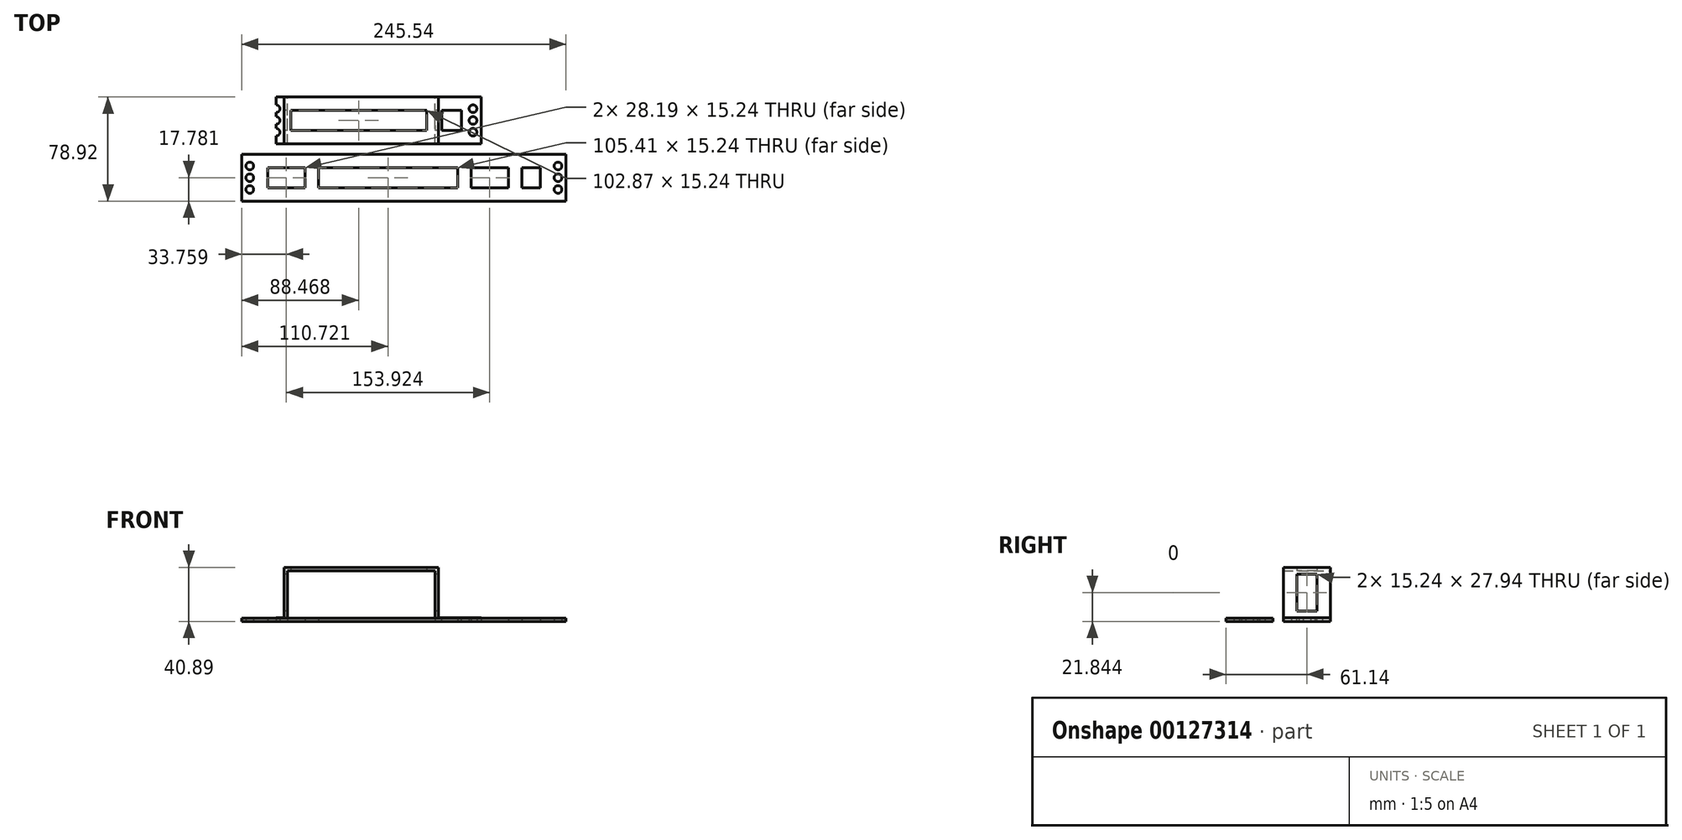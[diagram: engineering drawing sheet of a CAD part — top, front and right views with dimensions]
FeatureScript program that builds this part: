
annotation { "Feature Type Name" : "Feature", "Feature Type Description" : "" }
export const myFeature = defineFeature(function(context is Context, id is Id, definition is map)
    precondition{}
    {
        {
            var Q0;
            Q0=qCreatedBy(makeId("Top.planeOp"),FACE);
            var sketch = newSketch(context, id + "F0", { "sketchPlane" : qUnion([Q0])});
            skLineSegment(sketch, "E0.left", {"start": v(80.6, 17.78) * mm, "end": v(80.6, -17.78) * mm});
            skLineSegment(sketch, "E0.right", {"start": v(-80.6, 17.78) * mm, "end": v(-80.6, -17.78) * mm});
            skPoint(sketch, "E0.middle", {"position": v(0, 0) * mm});
            skLineSegment(sketch, "E1.left", {"start": v(66.03, 7.62) * mm, "end": v(66.03, -7.62) * mm});
            skLineSegment(sketch, "E1.right", {"start": v(-66.03, 7.62) * mm, "end": v(-66.03, -7.62) * mm});
            skLineSegment(sketch, "E2", {"start": v(-66.03, 7.62) * mm, "end": v(-66.03, 17.78) * mm});
            skLineSegment(sketch, "E3", {"start": v(-66.03, 17.78) * mm, "end": v(-66.03, -17.78) * mm});
            skLineSegment(sketch, "E4", {"start": v(66.03, 7.62) * mm, "end": v(66.03, 17.78) * mm});
            skLineSegment(sketch, "E5", {"start": v(66.03, 17.78) * mm, "end": v(66.03, -17.78) * mm});
            skLineSegment(sketch, "E6", {"start": v(-74.55, 17.78) * mm, "end": v(-74.55, -17.78) * mm});
            skLineSegment(sketch, "E7", {"start": v(-80.6, 0) * mm, "end": v(-80.6, -8.9) * mm});
            skCircle(sketch, "E8", {"center": v(-74.55, 8.9) * mm, "radius": 2.92 * mm});
            skCircle(sketch, "E9", {"center": v(-74.55, 0) * mm, "radius": 2.92 * mm});
            skCircle(sketch, "E10", {"center": v(-74.55, -8.9) * mm, "radius": 2.92 * mm});
            skCircle(sketch, "E11.MirrorC", {"center": v(74.55, 8.9) * mm, "radius": 2.92 * mm});
            skCircle(sketch, "E12.MirrorC", {"center": v(74.55, 0) * mm, "radius": 2.92 * mm});
            skCircle(sketch, "E13.MirrorC", {"center": v(74.55, -8.9) * mm, "radius": 2.92 * mm});
            skLineSegment(sketch, "E14", {"start": v(-80.6, 17.78) * mm, "end": v(-66.03, 17.78) * mm});
            skLineSegment(sketch, "E15", {"start": v(-66.03, -17.78) * mm, "end": v(-80.6, -17.78) * mm});
            skLineSegment(sketch, "E16", {"start": v(66.03, 17.78) * mm, "end": v(80.6, 17.78) * mm});
            skLineSegment(sketch, "E17", {"start": v(80.6, -17.78) * mm, "end": v(66.03, -17.78) * mm});
            skLineSegment(sketch, "E18.bottom", {"start": v(-66.03, 17.78) * mm, "end": v(66.03, 17.78) * mm});
            skLineSegment(sketch, "E18.top", {"start": v(-66.03, -17.78) * mm, "end": v(66.03, -17.78) * mm});
            skLineSegment(sketch, "E19.top", {"start": v(66.03, -7.62) * mm, "end": v(-66.03, -7.62) * mm});
            skLineSegment(sketch, "E20", {"start": v(39.38, 17.78) * mm, "end": v(39.38, -17.78) * mm});
            skLineSegment(sketch, "E21", {"start": v(-66.03, 7.62) * mm, "end": v(39.38, 7.62) * mm});
            skLineSegment(sketch, "E22", {"start": v(39.38, 7.62) * mm, "end": v(66.03, 7.62) * mm});
            skSolve(sketch);
        }
        {
            var Q0;
            {var subQ5=sQuery(id+"F0.wireOp",EDGE,"E21");Q0=makeQuery(id+"F0.imprint","IMPRINT",FACE,{"disambiguationData":[TD([[makeQuery(id+"F0.imprint","IMPRINT",EDGE,{"derivedFrom":subQ5}),1.0]])]});}
            var Q1;
            {var subQ8=sQuery(id+"F0.wireOp",EDGE,"E1.right");Q1=makeQuery(id+"F0.imprint","IMPRINT",FACE,{"disambiguationData":[TD([[makeQuery(id+"F0.imprint","IMPRINT",EDGE,{"derivedFrom":subQ8}),-1.0]])]});}
            var Q2;
            {var subQ1=sQuery(id+"F0.wireOp",EDGE,"E18.top");var subQ3=sQuery(id+"F0.wireOp",EDGE,"E20");var subQ4=makeQuery(id+"F0.imprint","INTERSECT",VERTEX,{"derivedFrom":[subQ1,subQ3]});Q2=makeQuery(id+"F0.imprint","IMPRINT",FACE,{"disambiguationData":[TD([[makeQuery(id+"F0.imprint","IMPRINT",EDGE,{"disambiguationData":[TD([[subQ4,1.0]])],"derivedFrom":subQ3}),-1.0]])]});}
            var Q3;
            {var subQ1=sQuery(id+"F0.wireOp",EDGE,"E18.top");var subQ3=sQuery(id+"F0.wireOp",EDGE,"E20");var subQ4=makeQuery(id+"F0.imprint","INTERSECT",VERTEX,{"derivedFrom":[subQ1,subQ3]});Q3=makeQuery(id+"F0.imprint","IMPRINT",FACE,{"disambiguationData":[TD([[makeQuery(id+"F0.imprint","IMPRINT",EDGE,{"disambiguationData":[TD([[subQ4,1.0]])],"derivedFrom":subQ3}),1.0]])]});}
            var Q4;
            {var subQ5=sQuery(id+"F0.wireOp",EDGE,"E22");Q4=makeQuery(id+"F0.imprint","IMPRINT",FACE,{"disambiguationData":[TD([[makeQuery(id+"F0.imprint","IMPRINT",EDGE,{"derivedFrom":subQ5}),1.0]])]});}
            var Q5;
            {var subQ0=sQuery(id+"F0.wireOp",EDGE,"E1.left");Q5=makeQuery(id+"F0.imprint","IMPRINT",FACE,{"disambiguationData":[TD([[makeQuery(id+"F0.imprint","IMPRINT",EDGE,{"derivedFrom":subQ0}),-1.0]])]});}
            var Q6;
            Q6=makeQuery(id+"F0.imprint","IMPRINT",FACE,{"disambiguationData":[TD([[makeQuery(id+"F0.imprint","IMPRINT",EDGE,{"derivedFrom":sQuery(id+"F0.wireOp",EDGE,"E0.left")}),-1.0]])]});
            var Q7;
            {var subQ14=sQuery(id+"F0.wireOp",EDGE,"E7");Q7=makeQuery(id+"F0.imprint","IMPRINT",FACE,{"disambiguationData":[TD([[makeQuery(id+"F0.imprint","IMPRINT",EDGE,{"derivedFrom":subQ14}),1.0]])]});}
            extrude(context, id + "F1", {"entities" : qUnion([Q0, Q1, Q2, Q3, Q4, Q5, Q6, Q7]), "depth" : 40.9 * mm});
        }
        {
            var Q0;
            Q0=makeQuery(id+"F1.opExtrude","CAP_FACE",FACE,{"disambiguationData":[OSD([sQuery(id+"F0.wireOp",EDGE,"E0.left"),sQuery(id+"F0.wireOp",EDGE,"E0.right"),sQuery(id+"F0.wireOp",EDGE,"E7"),sQuery(id+"F0.wireOp",EDGE,"E8"),sQuery(id+"F0.wireOp",EDGE,"E9"),sQuery(id+"F0.wireOp",EDGE,"E10"),sQuery(id+"F0.wireOp",EDGE,"E11.MirrorC"),sQuery(id+"F0.wireOp",EDGE,"E12.MirrorC"),sQuery(id+"F0.wireOp",EDGE,"E13.MirrorC"),sQuery(id+"F0.wireOp",EDGE,"E14"),sQuery(id+"F0.wireOp",EDGE,"E15"),sQuery(id+"F0.wireOp",EDGE,"E16"),sQuery(id+"F0.wireOp",EDGE,"E17"),sQuery(id+"F0.wireOp",EDGE,"E18.bottom"),sQuery(id+"F0.wireOp",EDGE,"E18.top"),sQuery(id+"F0.wireOp",EDGE,"E19.top"),sQuery(id+"F0.wireOp",EDGE,"E1.right"),sQuery(id+"F0.wireOp",EDGE,"E20"),sQuery(id+"F0.wireOp",EDGE,"E21")])],"isStart":false});
            var sketch = newSketch(context, id + "F2", { "sketchPlane" : qUnion([Q0])});
            skLineSegment(sketch, "E23", {"start": v(-68.57, 17.78) * mm, "end": v(-68.57, -17.78) * mm});
            skLineSegment(sketch, "E24", {"start": v(41.92, -17.78) * mm, "end": v(41.92, 17.78) * mm});
            skLineSegment(sketch, "E25", {"start": v(47, 17.78) * mm, "end": v(47, -17.78) * mm});
            skLineSegment(sketch, "E26", {"start": v(48.27, 17.78) * mm, "end": v(48.27, -17.78) * mm});
            skSolve(sketch);
        }
        {
            var Q0;
            Q0 = qSketchRegion(id + "F2", true);
            var Q1;
            {var subQ1=sQuery(id+"F2.wireOp",EDGE,"E23");Q1=makeQuery(id+"F2.imprint","IMPRINT",FACE,{"disambiguationData":[TD([[makeQuery(id+"F2.imprint","IMPRINT",EDGE,{"derivedFrom":subQ1}),-1.0]])]});}
            var Q2;
            {var subQ2=sQuery(id+"F2.wireOp",EDGE,"E26");Q2=makeQuery(id+"F2.imprint","IMPRINT",FACE,{"disambiguationData":[TD([[makeQuery(id+"F2.imprint","IMPRINT",EDGE,{"derivedFrom":subQ2}),1.0]])]});}
            extrude(context, id + "F3", {"entities" : qUnion([Q0, Q1, Q2]), "operationType" : NewBodyOperationType.REMOVE, "oppositeDirection" : true, "depth" : 38.1 * mm});
        }
        {
            var Q0;
            Q0=makeQuery(id+"F1.opExtrude","CAP_FACE",FACE,{"disambiguationData":[OSD([sQuery(id+"F0.wireOp",EDGE,"E0.left"),sQuery(id+"F0.wireOp",EDGE,"E0.right"),sQuery(id+"F0.wireOp",EDGE,"E7"),sQuery(id+"F0.wireOp",EDGE,"E8"),sQuery(id+"F0.wireOp",EDGE,"E9"),sQuery(id+"F0.wireOp",EDGE,"E10"),sQuery(id+"F0.wireOp",EDGE,"E11.MirrorC"),sQuery(id+"F0.wireOp",EDGE,"E12.MirrorC"),sQuery(id+"F0.wireOp",EDGE,"E13.MirrorC"),sQuery(id+"F0.wireOp",EDGE,"E14"),sQuery(id+"F0.wireOp",EDGE,"E15"),sQuery(id+"F0.wireOp",EDGE,"E16"),sQuery(id+"F0.wireOp",EDGE,"E17"),sQuery(id+"F0.wireOp",EDGE,"E18.bottom"),sQuery(id+"F0.wireOp",EDGE,"E18.top"),sQuery(id+"F0.wireOp",EDGE,"E19.top"),sQuery(id+"F0.wireOp",EDGE,"E1.right"),sQuery(id+"F0.wireOp",EDGE,"E20"),sQuery(id+"F0.wireOp",EDGE,"E21")])],"isStart":true});
            var sketch = newSketch(context, id + "F4", { "sketchPlane" : qUnion([Q0])});
            skLineSegment(sketch, "E27", {"start": v(-66.03, 7.62) * mm, "end": v(-66.03, 17.78) * mm});
            skLineSegment(sketch, "E28", {"start": v(39.38, 7.62) * mm, "end": v(39.38, 17.78) * mm});
            skLineSegment(sketch, "E29", {"start": v(39.38, 17.78) * mm, "end": v(39.38, -17.78) * mm});
            skLineSegment(sketch, "E30", {"start": v(-66.03, 17.78) * mm, "end": v(-66.03, -17.78) * mm});
            skLineSegment(sketch, "E31", {"start": v(44.46, 17.78) * mm, "end": v(44.46, -17.78) * mm});
            skLineSegment(sketch, "E32", {"start": v(45.73, 17.78) * mm, "end": v(45.73, -17.78) * mm});
            skSolve(sketch);
        }
        {
            var Q0;
            Q0 = qSketchRegion(id + "F4", true);
            var Q1;
            {var subQ1=makeQuery(id+"F1.opExtrude","CAP_EDGE",EDGE,{"disambiguationData":[OSD([sQuery(id+"F0.wireOp",EDGE,"E19.top")])],"isStart":true});Q1=makeQuery(id+"F4.imprint","IMPRINT",FACE,{"disambiguationData":[TD([[makeQuery(id+"F4.imprint","IMPRINT",EDGE,{"derivedFrom":subQ1}),-1.0]])]});}
            var Q2;
            {var subQ1=makeQuery(id+"F1.opExtrude","CAP_EDGE",EDGE,{"disambiguationData":[OSD([sQuery(id+"F0.wireOp",EDGE,"E21")])],"isStart":true});Q2=makeQuery(id+"F4.imprint","IMPRINT",FACE,{"disambiguationData":[TD([[makeQuery(id+"F4.imprint","IMPRINT",EDGE,{"derivedFrom":subQ1}),-1.0]])]});}
            var Q3;
            {var subQ3=sQuery(id+"F4.wireOp",EDGE,"E31");Q3=makeQuery(id+"F4.imprint","IMPRINT",FACE,{"disambiguationData":[TD([[makeQuery(id+"F4.imprint","IMPRINT",EDGE,{"derivedFrom":subQ3}),-1.0]])]});}
            var Q4;
            {var subQ0=sQuery(id+"F4.wireOp",EDGE,"E31");Q4=makeQuery(id+"F4.imprint","IMPRINT",FACE,{"disambiguationData":[TD([[makeQuery(id+"F4.imprint","IMPRINT",EDGE,{"derivedFrom":subQ0}),1.0]])]});}
            extrude(context, id + "F5", {"entities" : qUnion([Q0, Q1, Q2, Q3, Q4]), "operationType" : NewBodyOperationType.REMOVE, "oppositeDirection" : true, "depth" : 38.35 * mm});
        }
        {
            var Q0;
            Q0=makeQuery(id+"F3.boolean.opBoolean","COPY",FACE,{"derivedFrom":makeQuery(id+"F3.opExtrude","SWEPT_FACE",FACE,{"disambiguationData":[OSD([sQuery(id+"F2.wireOp",EDGE,"E23")])]})});
            var sketch = newSketch(context, id + "F6", { "sketchPlane" : qUnion([Q0])});
            skLineSegment(sketch, "E33.bottom", {"start": v(-7.62, 35.81) * mm, "end": v(7.62, 35.81) * mm});
            skLineSegment(sketch, "E33.top", {"start": v(-7.62, 7.87) * mm, "end": v(7.62, 7.87) * mm});
            skLineSegment(sketch, "E33.left", {"start": v(-7.62, 35.81) * mm, "end": v(-7.62, 7.87) * mm});
            skLineSegment(sketch, "E33.right", {"start": v(7.62, 35.81) * mm, "end": v(7.62, 7.87) * mm});
            skSolve(sketch);
        }
        {
            var Q0;
            Q0 = qSketchRegion(id + "F6", true);
            extrude(context, id + "F7", {"entities" : qUnion([Q0]), "operationType" : NewBodyOperationType.REMOVE, "endBound" : BoundingType.THROUGH_ALL, "oppositeDirection" : true, "depth" : 25.4 * mm});
        }
        {
            var Q0;
            Q0=makeQuery(id+"F3.boolean.opBoolean","COPY",FACE,{"derivedFrom":makeQuery(id+"F3.opExtrude","CAP_FACE",FACE,{"disambiguationData":[OSD([sQuery(id+"F0.wireOp",EDGE,"E0.left"),sQuery(id+"F0.wireOp",EDGE,"E11.MirrorC"),sQuery(id+"F0.wireOp",EDGE,"E12.MirrorC"),sQuery(id+"F0.wireOp",EDGE,"E13.MirrorC"),sQuery(id+"F0.wireOp",EDGE,"E14"),sQuery(id+"F0.wireOp",EDGE,"E15"),sQuery(id+"F0.wireOp",EDGE,"E16"),sQuery(id+"F0.wireOp",EDGE,"E17"),sQuery(id+"F0.wireOp",EDGE,"E18.bottom"),sQuery(id+"F0.wireOp",EDGE,"E18.top"),sQuery(id+"F2.wireOp",EDGE,"E24")])],"isStart":false})});
            var sketch = newSketch(context, id + "F8", { "sketchPlane" : qUnion([Q0])});
            skLineSegment(sketch, "E34.bottom", {"start": v(50.81, 7.62) * mm, "end": v(65.77, 7.62) * mm});
            skLineSegment(sketch, "E34.top", {"start": v(50.81, -7.62) * mm, "end": v(65.77, -7.62) * mm});
            skLineSegment(sketch, "E34.left", {"start": v(50.81, 7.62) * mm, "end": v(50.81, -7.62) * mm});
            skLineSegment(sketch, "E34.right", {"start": v(65.77, 7.62) * mm, "end": v(65.77, -7.62) * mm});
            skSolve(sketch);
        }
        {
            var Q0;
            Q0=makeQuery(id+"F8.imprint","IMPRINT",FACE,{"disambiguationData":[TD([[makeQuery(id+"F8.imprint","IMPRINT",EDGE,{"derivedFrom":sQuery(id+"F8.wireOp",EDGE,"E34.bottom")}),-1.0]])]});
            extrude(context, id + "F9", {"entities" : qUnion([Q0]), "operationType" : NewBodyOperationType.REMOVE, "oppositeDirection" : true, "depth" : 5.08 * mm});
        }
        {
            var Q0;
            Q0=qCreatedBy(makeId("Top.planeOp"),FACE);
            var sketch = newSketch(context, id + "F10", { "sketchPlane" : qUnion([Q0])});
            skLineSegment(sketch, "E35.bottom", {"start": v(-100.52, -61.14) * mm, "end": v(145.02, -61.14) * mm});
            skLineSegment(sketch, "E35.top", {"start": v(-100.52, -25.58) * mm, "end": v(145.02, -25.58) * mm});
            skLineSegment(sketch, "E35.left", {"start": v(-100.52, -61.14) * mm, "end": v(-100.52, -25.58) * mm});
            skLineSegment(sketch, "E35.right", {"start": v(145.02, -61.14) * mm, "end": v(145.02, -25.58) * mm});
            skLineSegment(sketch, "E36", {"start": v(-100.52, -25.58) * mm, "end": v(-85.94, -25.58) * mm});
            skLineSegment(sketch, "E37", {"start": v(-85.94, -25.58) * mm, "end": v(-85.94, -61.14) * mm});
            skLineSegment(sketch, "E38", {"start": v(130.44, -61.14) * mm, "end": v(130.44, -25.58) * mm});
            skCircle(sketch, "E39", {"center": v(-94.45, -34.47) * mm, "radius": 2.92 * mm});
            skCircle(sketch, "E40", {"center": v(-94.45, -43.36) * mm, "radius": 2.92 * mm});
            skCircle(sketch, "E41", {"center": v(-94.45, -52.25) * mm, "radius": 2.92 * mm});
            skCircle(sketch, "E42", {"center": v(138.95, -34.47) * mm, "radius": 2.92 * mm});
            skCircle(sketch, "E43", {"center": v(138.95, -43.36) * mm, "radius": 2.92 * mm});
            skCircle(sketch, "E44", {"center": v(138.95, -52.25) * mm, "radius": 2.92 * mm});
            skLineSegment(sketch, "E45", {"start": v(-47.58, -25.58) * mm, "end": v(-47.58, -61.14) * mm});
            skLineSegment(sketch, "E46", {"start": v(67.99, -25.58) * mm, "end": v(67.99, -61.14) * mm});
            skLineSegment(sketch, "E47", {"start": v(106.34, -25.58) * mm, "end": v(106.34, -61.14) * mm});
            skLineSegment(sketch, "E48.bottom", {"start": v(-80.86, -35.74) * mm, "end": v(-52.66, -35.74) * mm});
            skLineSegment(sketch, "E48.top", {"start": v(-80.86, -50.98) * mm, "end": v(-52.66, -50.98) * mm});
            skLineSegment(sketch, "E48.left", {"start": v(-80.86, -35.74) * mm, "end": v(-80.86, -50.98) * mm});
            skLineSegment(sketch, "E48.right", {"start": v(-52.66, -35.74) * mm, "end": v(-52.66, -50.98) * mm});
            skLineSegment(sketch, "E49.bottom", {"start": v(-42.5, -35.74) * mm, "end": v(62.9, -35.74) * mm});
            skLineSegment(sketch, "E49.top", {"start": v(-42.5, -50.98) * mm, "end": v(62.9, -50.98) * mm});
            skLineSegment(sketch, "E49.left", {"start": v(-42.5, -35.74) * mm, "end": v(-42.5, -50.98) * mm});
            skLineSegment(sketch, "E49.right", {"start": v(62.9, -35.74) * mm, "end": v(62.9, -50.98) * mm});
            skLineSegment(sketch, "E50.bottom", {"start": v(73.07, -35.74) * mm, "end": v(101.26, -35.74) * mm});
            skLineSegment(sketch, "E50.top", {"start": v(73.07, -50.98) * mm, "end": v(101.26, -50.98) * mm});
            skLineSegment(sketch, "E50.left", {"start": v(73.07, -35.74) * mm, "end": v(73.07, -50.98) * mm});
            skLineSegment(sketch, "E50.right", {"start": v(101.26, -35.74) * mm, "end": v(101.26, -50.98) * mm});
            skLineSegment(sketch, "E51.bottom", {"start": v(111.42, -35.74) * mm, "end": v(125.36, -35.74) * mm});
            skLineSegment(sketch, "E51.top", {"start": v(111.42, -50.98) * mm, "end": v(125.36, -50.98) * mm});
            skLineSegment(sketch, "E51.left", {"start": v(111.42, -35.74) * mm, "end": v(111.42, -50.98) * mm});
            skLineSegment(sketch, "E51.right", {"start": v(125.36, -35.74) * mm, "end": v(125.36, -50.98) * mm});
            skSolve(sketch);
        }
        {
            var Q0;
            Q0 = qSketchRegion(id + "F10", true);
            extrude(context, id + "F11", {"entities" : qUnion([Q0]), "depth" : 2.54 * mm});
        }
        {
            var Q0;
            {var subQ0=sQuery(id+"F4.wireOp",EDGE,"E30");Q0=makeQuery(id+"F5.boolean.opBoolean","MERGE",FACE,{"derivedFrom":[makeQuery(id+"F1.opExtrude","SWEPT_FACE",FACE,{"disambiguationData":[OSD([sQuery(id+"F0.wireOp",EDGE,"E1.right")])]}),makeQuery(id+"F5.opExtrude","SWEPT_FACE",FACE,{"disambiguationData":[OSD([subQ0]),TDD([makeQuery(id+"F4.imprint","IMPRINT",EDGE,{"disambiguationData":[TD([[makeQuery(id+"F4.imprint","INTERSECT",VERTEX,{"derivedFrom":[makeQuery(id+"F1.opExtrude","CAP_EDGE",EDGE,{"disambiguationData":[OSD([sQuery(id+"F0.wireOp",EDGE,"E19.top")])],"isStart":true}),subQ0]}),1.0],[makeQuery(id+"F4.imprint","INTERSECT",VERTEX,{"derivedFrom":[makeQuery(id+"F1.opExtrude","CAP_EDGE",EDGE,{"disambiguationData":[OSD([sQuery(id+"F0.wireOp",EDGE,"E15"),sQuery(id+"F0.wireOp",EDGE,"E17"),sQuery(id+"F0.wireOp",EDGE,"E18.top")])],"isStart":true}),subQ0]}),-1.0]])],"derivedFrom":subQ0})])]}),makeQuery(id+"F5.opExtrude","SWEPT_FACE",FACE,{"disambiguationData":[OSD([subQ0]),TDD([makeQuery(id+"F4.imprint","IMPRINT",EDGE,{"disambiguationData":[TD([[makeQuery(id+"F4.imprint","INTERSECT",VERTEX,{"derivedFrom":[makeQuery(id+"F1.opExtrude","CAP_EDGE",EDGE,{"disambiguationData":[OSD([sQuery(id+"F0.wireOp",EDGE,"E21")])],"isStart":true}),subQ0]}),-1.0],[makeQuery(id+"F4.imprint","INTERSECT",VERTEX,{"derivedFrom":[makeQuery(id+"F1.opExtrude","CAP_EDGE",EDGE,{"disambiguationData":[OSD([sQuery(id+"F0.wireOp",EDGE,"E14"),sQuery(id+"F0.wireOp",EDGE,"E16"),sQuery(id+"F0.wireOp",EDGE,"E18.bottom")])],"isStart":true}),subQ0]}),1.0]])],"derivedFrom":subQ0})])]})]});}
            var sketch = newSketch(context, id + "F12", { "sketchPlane" : qUnion([Q0])});
            skLineSegment(sketch, "E52.bottom", {"start": v(7.62, 38.35) * mm, "end": v(-7.62, 38.35) * mm});
            skLineSegment(sketch, "E52.top", {"start": v(7.62, 40.9) * mm, "end": v(-7.62, 40.9) * mm});
            skLineSegment(sketch, "E52.left", {"start": v(7.62, 38.35) * mm, "end": v(7.62, 40.9) * mm});
            skLineSegment(sketch, "E52.right", {"start": v(-7.62, 38.35) * mm, "end": v(-7.62, 40.9) * mm});
            skSolve(sketch);
        }
        {
            var Q0;
            Q0 = qSketchRegion(id + "F12", true);
            extrude(context, id + "F13", {"entities" : qUnion([Q0]), "operationType" : NewBodyOperationType.ADD, "depth" : 2.54 * mm});
        }
    });
